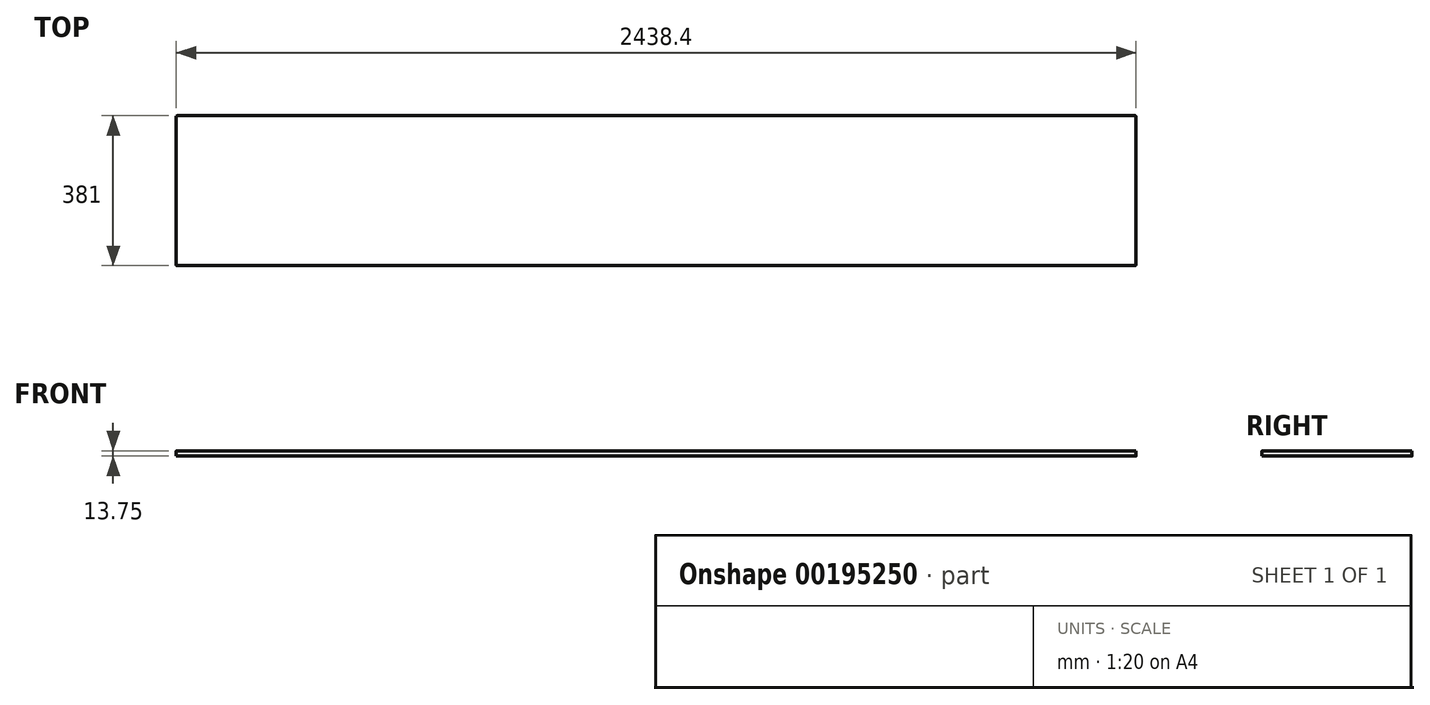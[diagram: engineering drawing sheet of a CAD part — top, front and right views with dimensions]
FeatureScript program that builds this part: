
annotation { "Feature Type Name" : "Feature", "Feature Type Description" : "" }
export const myFeature = defineFeature(function(context is Context, id is Id, definition is map)
    precondition{}
    {
        {
            var Q0;
            Q0=qCreatedBy(makeId("Top.planeOp"),FACE);
            var sketch = newSketch(context, id + "F0", { "sketchPlane" : qUnion([Q0])});
            skLineSegment(sketch, "E0.bottom", {"start": v(-1219.2, -190.5) * mm, "end": v(1219.2, -190.5) * mm});
            skLineSegment(sketch, "E0.top", {"start": v(-1219.2, 190.5) * mm, "end": v(1219.2, 190.5) * mm});
            skLineSegment(sketch, "E0.left", {"start": v(-1219.2, -190.5) * mm, "end": v(-1219.2, 190.5) * mm});
            skLineSegment(sketch, "E0.right", {"start": v(1219.2, -190.5) * mm, "end": v(1219.2, 190.5) * mm});
            skPoint(sketch, "E0.middle", {"position": v(0, 0) * mm});
            skSolve(sketch);
        }
        {
            var Q0;
            Q0=makeQuery(id+"F0.imprint","IMPRINT",FACE,{"disambiguationData":[TD([[makeQuery(id+"F0.imprint","IMPRINT",EDGE,{"derivedFrom":sQuery(id+"F0.wireOp",EDGE,"E0.bottom")}),1.0]])]});
            extrude(context, id + "F1", {"entities" : qUnion([Q0]), "depth" : 13.75 * mm});
        }
        {
            var Q0;
            Q0=makeQuery(id+"F1.opExtrude","SWEPT_EDGE",EDGE,{"disambiguationData":[OSD([sQuery(id+"F0.wireOp",EDGE,"E0.bottom"),sQuery(id+"F0.wireOp",EDGE,"E0.right")])]});
            var Q1;
            Q1=makeQuery(id+"F1.opExtrude","SWEPT_EDGE",EDGE,{"disambiguationData":[OSD([sQuery(id+"F0.wireOp",EDGE,"E0.top"),sQuery(id+"F0.wireOp",EDGE,"E0.right")])]});
            var Q2;
            Q2=makeQuery(id+"F1.opExtrude","SWEPT_EDGE",EDGE,{"disambiguationData":[OSD([sQuery(id+"F0.wireOp",EDGE,"E0.bottom"),sQuery(id+"F0.wireOp",EDGE,"E0.left")])]});
            var Q3;
            Q3=makeQuery(id+"F1.opExtrude","SWEPT_EDGE",EDGE,{"disambiguationData":[OSD([sQuery(id+"F0.wireOp",EDGE,"E0.top"),sQuery(id+"F0.wireOp",EDGE,"E0.left")])]});
            fillet(context, id + "F2", {"entities" : qUnion([Q0, Q1, Q2, Q3]), "radius" : 2 * mm, "tangentPropagation" : true, "allowEdgeOverflow" : false});
        }
    });
